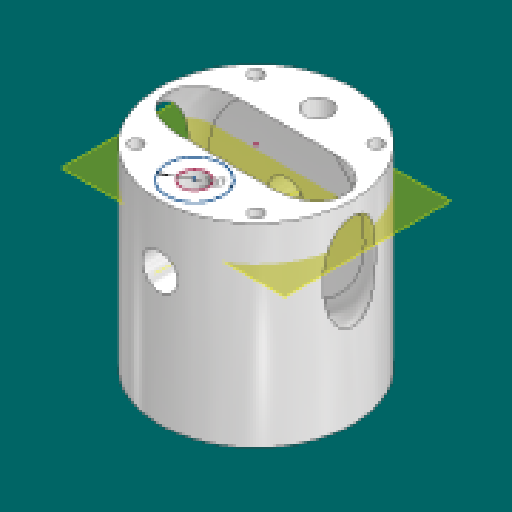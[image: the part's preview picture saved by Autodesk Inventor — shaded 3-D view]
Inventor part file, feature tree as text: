
AUTODESK INVENTOR PART (.ipt)
format: ipt  version: 2023.1 (Build 271208000, 208)  size: 1,229,824 bytes
history: native  units: in
note: dims shown in document units (in); Inventor stores cm internally (conversion verified against a paired STEP export)
features: sketch x13, extrude x11, fillet x10, chamfer x3, mirror x3, projected_geometry x3, plane x2, draft x2, revolve x1, other x1
ambient origin geometry x8: Origin, YZ Plane, XZ Plane, XY Plane, X Axis, Y Axis, Z Axis, Center Point
bodies: Solid1 (feature_tree)
feature tree (49):
  extrude  "Extrusion1"  Depth=0.5in
  revolve  "Revolution1"  Angle=45.0deg
  other  "Work Axis3"
  extrude  "Extrusion3"  Depth=0.375in
  plane  "Work Plane2"
  extrude  "Extrusion6"  Depth=2.75in
  extrude  "Extrusion7"  Depth=2.25in
  extrude  "Extrusion12"  Depth=0.4331in
  chamfer  "Chamfer1"  [1 undecoded]
  draft  "FaceDraft1"
  chamfer  "Chamfer2"  Distance=0.3125in
  draft  "FaceDraft2"
  fillet  "Fillet2"  [1 undecoded]
  fillet  "Fillet3"  Radius=1.0in
  mirror  "Mirror1"
  extrude  "Extrusion8"  Depth=0.0787in TaperAngle=45.0deg
  extrude  "Extrusion9"  Depth=0.481in
  extrude  "Extrusion10"  Depth=0.0787in TaperAngle=45.0deg
  extrude  "Extrusion11"  Depth=0.481in
  fillet  "Fillet4"  Radius=0.0394in
  fillet  "Fillet8"  Radius=0.0394in
  fillet  "Fillet9"  Radius=1.125in
  mirror  "Mirror7"
  fillet  "Fillet10"  Radius=0.15in
  sketch  "Sketch18"  dims[d53=0.75in]
  extrude  "Extrusion13"  Depth=1.25in
  plane  "Work Plane3"
  extrude  "Extrusion14"  Depth=2.75in
  fillet  "Fillet11"  Radius=1.0in
  mirror  "Mirror8"
  fillet  "Fillet12"  [1 undecoded]
  fillet  "Fillet13"  [1 undecoded]
  fillet  "Fillet14"  Radius=0.1875in
  chamfer  "Chamfer3"  [1 undecoded]
  sketch  "Sketch1"  dims[d1=0.1875in d2=0.5in]
  sketch  "Sketch3"  dims[d3=0.0787in d4=45.0deg]
  sketch  "Sketch6"  dims[d5=1.5748in d7=360.0deg d10=0.375in]
  sketch  "Sketch11"  dims[d11=2.75in d12=0.0in d22=2.75in]
  sketch  "Sketch12"  dims[d23=0.1181in d24=2.25in]
  sketch  "Sketch13"  dims[d26=360.0deg d29=0.4331in]
  sketch  "Sketch14"  dims[d37=2.75in d40=0.0in d41=0.0in]
  sketch  "Sketch16"  dims[d42=0.5in]
  projected_geometry  "Projected Loop1"
  sketch  "Sketch17"  dims[d49=-0.3125in]
  projected_geometry  "Projected Loop2"
  sketch  "Sketch19"  dims[d54=0.5in]
  projected_geometry  "Projected Loop3"
  sketch  "Sketch20"  dims[d55=2.8346in]
  sketch  "Sketch21"  dims[d56=1.063in d57=0.3125in d58=0.0in d60=45.0deg d61=1.0in d62=0.0in d63=0.0787in d64=0.125in d65=45.0deg d66=0.481in d68=0.0787in d69=0.125in d70=45.0deg d71=0.481in d72=0.0394in d73=0.0394in d74=1.125in d75=0.15in d76=-0.3092in d77=1.25in d78=2.75in d79=1.0in d80=45.0deg d81=0.0in d82=0.0in d83=0.1875in d84=0.0in d85=0.0in d86=0.25in d87=0.0in d88=0.0in d89=0.0394in d93=0.0394in d94=0.0394in d95=0.0394in d96=1.75in d97=0.0in d98=0.5in d99=0.0in d100=0.0in d101=-0.196in d102=0.5in d103=0.4in d104=1.0in d105=0.0in d106=0.0394in d112=0.25in d113=0.25in d114=0.0394in d115=0.0236in d116=0.125in d117=45.0deg d67=0.0344in]
note: 5 required parameter values undecoded (feature->parameter linkage not recoverable at this tier; creation-order binding heuristic only, values carry confidence <= 0.55)
